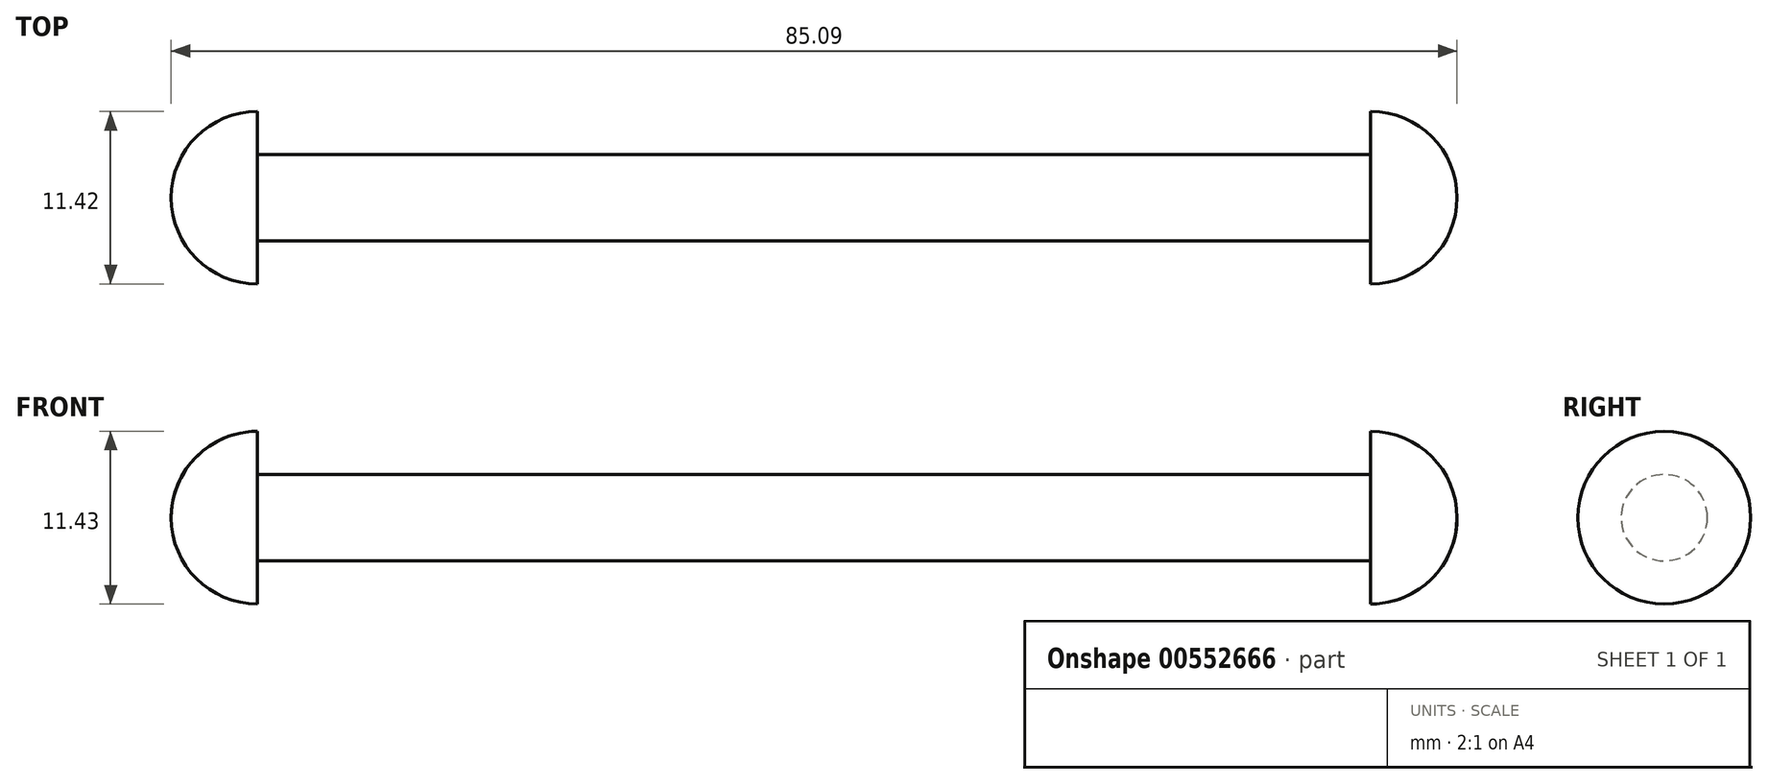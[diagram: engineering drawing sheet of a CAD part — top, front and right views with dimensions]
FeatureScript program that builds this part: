
annotation { "Feature Type Name" : "Feature", "Feature Type Description" : "" }
export const myFeature = defineFeature(function(context is Context, id is Id, definition is map)
    precondition{}
    {
        {
            var Q0;
            Q0=qCreatedBy(makeId("Front.planeOp"),FACE);
            var sketch = newSketch(context, id + "F0", { "sketchPlane" : qUnion([Q0])});
            skArc(sketch, "E0", {"start": v(-42.89, 5.72) * mm, "mid": v(-46.93, 4.04) * mm, "end": v(-48.6, 0) * mm});
            skLineSegment(sketch, "E1", {"start": v(-42.89, 2.86) * mm, "end": v(-42.89, 5.71) * mm});
            skLineSegment(sketch, "E2", {"start": v(-42.89, 2.86) * mm, "end": v(30.77, 2.86) * mm});
            skLineSegment(sketch, "E3", {"start": v(-42.89, 0) * mm, "end": v(-48.6, 0) * mm});
            skLineSegment(sketch, "E4", {"start": v(-48.6, 0) * mm, "end": v(-37.17, 0) * mm});
            skLineSegment(sketch, "E5.MirrorCS", {"start": v(30.77, 0) * mm, "end": v(36.49, 0) * mm});
            skArc(sketch, "E6.MirrorCS", {"start": v(30.77, 5.72) * mm, "mid": v(34.82, 4.04) * mm, "end": v(36.49, 0) * mm});
            skLineSegment(sketch, "E7.MirrorCS", {"start": v(30.77, 2.86) * mm, "end": v(30.77, 5.71) * mm});
            skPoint(sketch, "E8.MirrorCS.end.orphan", {"position": v(-48.6, 0) * mm});
            skPoint(sketch, "E9.orphan", {"position": v(-42.89, -2.86) * mm});
            skPoint(sketch, "E10.orphan", {"position": v(-42.89, -5.71) * mm});
            skPoint(sketch, "E11.MirrorCS.end.orphan", {"position": v(30.77, -2.86) * mm});
            skPoint(sketch, "E12.start.orphan", {"position": v(-6.06, 2.86) * mm});
            skLineSegment(sketch, "E13", {"start": v(-37.17, 0) * mm, "end": v(30.77, 0) * mm});
            skSolve(sketch);
        }
        {
            var Q0;
            Q0 = qSketchRegion(id + "F0", true);
            var Q1;
            Q1=sQuery(id+"F0.wireOp",EDGE,"E13");
            revolve(context, id + "F1", {"entities" : qUnion([Q0]), "axis" : qUnion([Q1]), "revolveType" : RevolveType.FULL});
        }
    });
